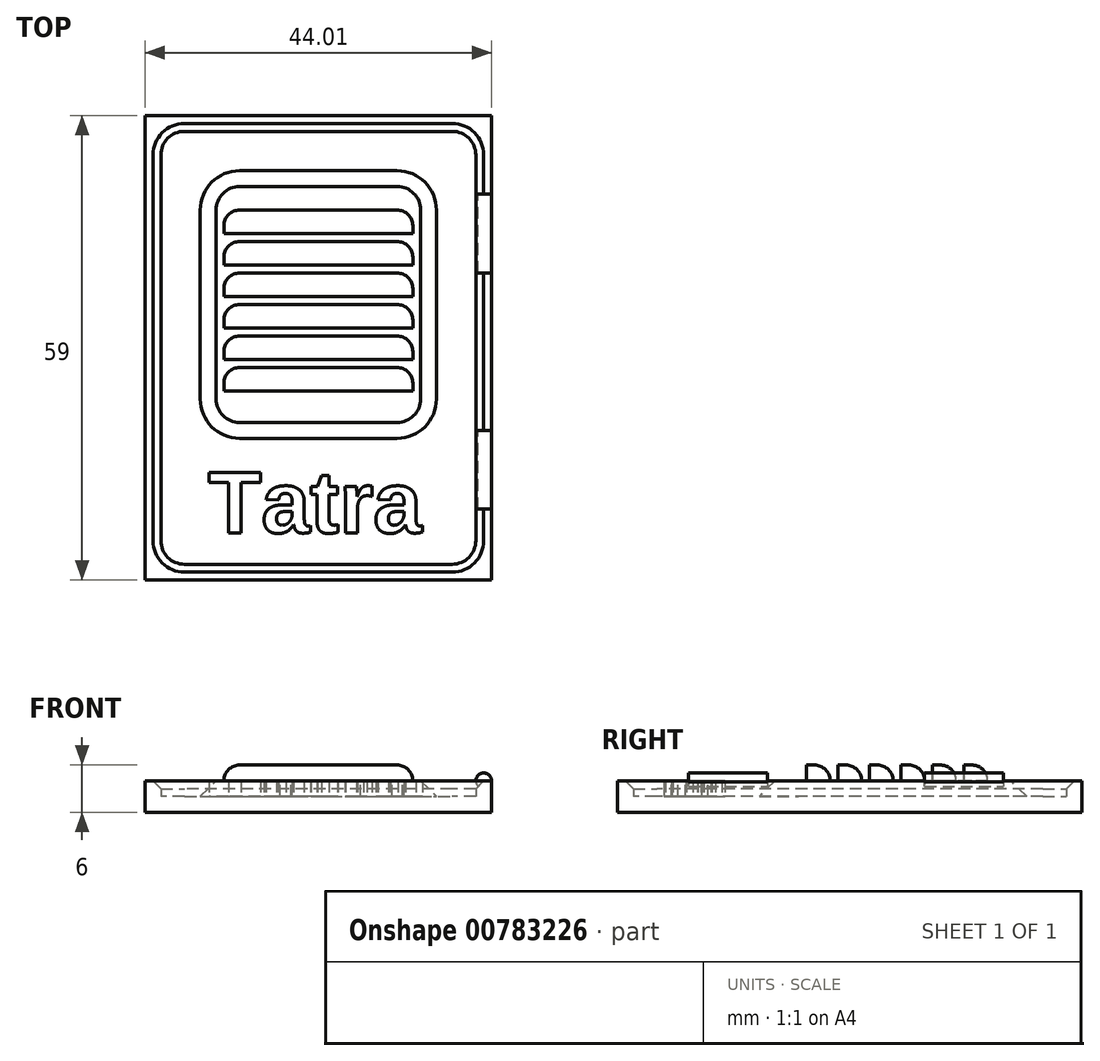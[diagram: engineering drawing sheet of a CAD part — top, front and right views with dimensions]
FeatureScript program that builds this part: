
annotation { "Feature Type Name" : "Feature", "Feature Type Description" : "" }
export const myFeature = defineFeature(function(context is Context, id is Id, definition is map)
    precondition{}
    {
        {
            var Q0;
            Q0=qCreatedBy(makeId("Top.planeOp"),FACE);
            var sketch = newSketch(context, id + "F0", { "sketchPlane" : qUnion([Q0])});
            skLineSegment(sketch, "E0.bottom", {"start": v(-26.46, 17) * mm, "end": v(17.54, 17) * mm});
            skLineSegment(sketch, "E0.top", {"start": v(-26.46, -42) * mm, "end": v(17.54, -42) * mm});
            skLineSegment(sketch, "E0.left", {"start": v(-26.46, 17) * mm, "end": v(-26.46, -42) * mm});
            skLineSegment(sketch, "E0.right", {"start": v(17.54, 17) * mm, "end": v(17.54, -42) * mm});
            skSolve(sketch);
        }
        {
            var Q0;
            Q0 = qSketchRegion(id + "F0", true);
            extrude(context, id + "F1", {"entities" : qUnion([Q0]), "depth" : 2 * mm, "offsetDistance" : 25 * mm});
        }
        {
            var Q0;
            Q0=makeQuery(id+"F1.opExtrude","CAP_FACE",FACE,{"disambiguationData":[OSD([sQuery(id+"F0.wireOp",EDGE,"E0.bottom"),sQuery(id+"F0.wireOp",EDGE,"E0.top"),sQuery(id+"F0.wireOp",EDGE,"E0.left"),sQuery(id+"F0.wireOp",EDGE,"E0.right")])],"isStart":false});
            var sketch = newSketch(context, id + "F2", { "sketchPlane" : qUnion([Q0])});
            skLineSegment(sketch, "E1.bottom", {"start": v(-26.46, 17) * mm, "end": v(17.54, 17) * mm});
            skLineSegment(sketch, "E1.top", {"start": v(-26.46, -42) * mm, "end": v(17.54, -42) * mm});
            skLineSegment(sketch, "E1.left", {"start": v(-26.46, 17) * mm, "end": v(-26.46, -42) * mm});
            skLineSegment(sketch, "E1.right", {"start": v(17.54, 17) * mm, "end": v(17.54, -42) * mm});
            skLineSegment(sketch, "E2.0", {"start": v(-24.46, 15) * mm, "end": v(-24.46, -40) * mm});
            skLineSegment(sketch, "E3.0", {"start": v(-24.46, 15) * mm, "end": v(15.54, 15) * mm});
            skLineSegment(sketch, "E4.0", {"start": v(15.54, 15) * mm, "end": v(15.54, -40) * mm});
            skLineSegment(sketch, "E5.0", {"start": v(-24.46, -40) * mm, "end": v(15.54, -40) * mm});
            skPoint(sketch, "E6", {"position": v(15.54, -22.21) * mm});
            skText(sketch, "E7", { "text": "Tatra", "fontName": "Arimo-Bold.ttf"});
            const initialGuessF2  = {"E7": [-0.02196, -0.038, 1, 0, 0.01]};
            skSetInitialGuess(sketch, initialGuessF2);
            skSolve(sketch);
        }
        {
            var Q0;
            Q0 = qSketchRegion(id + "F2", true);
            extrude(context, id + "F3", {"entities" : qUnion([Q0]), "operationType" : NewBodyOperationType.ADD, "depth" : 2 * mm, "offsetDistance" : 25 * mm});
        }
        {
            var Q0;
            Q0=makeQuery(id+"F1.opExtrude","CAP_FACE",FACE,{"disambiguationData":[OSD([sQuery(id+"F0.wireOp",EDGE,"E0.bottom"),sQuery(id+"F0.wireOp",EDGE,"E0.top"),sQuery(id+"F0.wireOp",EDGE,"E0.left"),sQuery(id+"F0.wireOp",EDGE,"E0.right")])],"isStart":false});
            var sketch = newSketch(context, id + "F4", { "sketchPlane" : qUnion([Q0])});
            skLineSegment(sketch, "E8.bottom", {"start": v(-14.46, 10) * mm, "end": v(5.54, 10) * mm});
            skLineSegment(sketch, "E8.top", {"start": v(-14.46, -24) * mm, "end": v(5.54, -24) * mm});
            skLineSegment(sketch, "E8.left", {"start": v(-19.46, 5) * mm, "end": v(-19.46, -19) * mm});
            skLineSegment(sketch, "E8.right", {"start": v(10.54, 5) * mm, "end": v(10.54, -19) * mm});
            skPoint(sketch, "E9.visualSharp", {"position": v(-19.46, 10) * mm});
            skArc(sketch, "E9.filletArc", {"start": v(-14.46, 10) * mm, "mid": v(-18, 8.53) * mm, "end": v(-19.46, 5) * mm});
            skPoint(sketch, "E10.visualSharp", {"position": v(10.54, 10) * mm});
            skArc(sketch, "E10.filletArc", {"start": v(10.54, 5) * mm, "mid": v(9.08, 8.53) * mm, "end": v(5.54, 10) * mm});
            skPoint(sketch, "E11.visualSharp", {"position": v(10.54, -24) * mm});
            skArc(sketch, "E11.filletArc", {"start": v(5.54, -24) * mm, "mid": v(9.08, -22.54) * mm, "end": v(10.54, -19) * mm});
            skPoint(sketch, "E12.visualSharp", {"position": v(-19.46, -24) * mm});
            skArc(sketch, "E12.filletArc", {"start": v(-19.46, -19) * mm, "mid": v(-18, -22.54) * mm, "end": v(-14.46, -24) * mm});
            skSolve(sketch);
        }
        {
            var Q0;
            Q0=makeQuery(id+"F4.imprint","IMPRINT",FACE,{"disambiguationData":[TD([[makeQuery(id+"F4.imprint","IMPRINT",EDGE,{"derivedFrom":sQuery(id+"F4.wireOp",EDGE,"E8.bottom")}),-1.0]])]});
            extrude(context, id + "F5", {"entities" : qUnion([Q0]), "operationType" : NewBodyOperationType.ADD, "depth" : 2 * mm, "offsetDistance" : 25 * mm});
        }
        {
            var Q0;
            Q0=makeQuery(id+"F5.opExtrude","CAP_FACE",FACE,{"disambiguationData":[OSD([sQuery(id+"F4.wireOp",EDGE,"E8.bottom"),sQuery(id+"F4.wireOp",EDGE,"E8.top"),sQuery(id+"F4.wireOp",EDGE,"E8.left"),sQuery(id+"F4.wireOp",EDGE,"E8.right"),sQuery(id+"F4.wireOp",EDGE,"E9.filletArc"),sQuery(id+"F4.wireOp",EDGE,"E10.filletArc"),sQuery(id+"F4.wireOp",EDGE,"E11.filletArc"),sQuery(id+"F4.wireOp",EDGE,"E12.filletArc")])],"isStart":false});
            var sketch = newSketch(context, id + "F6", { "sketchPlane" : qUnion([Q0])});
            skLineSegment(sketch, "E13.bottom", {"start": v(-14.46, 5) * mm, "end": v(5.54, 5) * mm});
            skLineSegment(sketch, "E13.left", {"start": v(-16.46, 3) * mm, "end": v(-16.46, 2) * mm});
            skLineSegment(sketch, "E13.right", {"start": v(7.54, 3) * mm, "end": v(7.54, 2) * mm});
            skLineSegment(sketch, "E14.0", {"start": v(-14.46, 1) * mm, "end": v(5.54, 1) * mm});
            skLineSegment(sketch, "E15.0", {"start": v(-14.46, -3) * mm, "end": v(5.54, -3) * mm});
            skLineSegment(sketch, "E16.0", {"start": v(-14.46, -7) * mm, "end": v(5.54, -7) * mm});
            skLineSegment(sketch, "E17.0", {"start": v(-14.46, -11) * mm, "end": v(5.54, -11) * mm});
            skPoint(sketch, "E18", {"position": v(-16.46, 1) * mm});
            skPoint(sketch, "E19", {"position": v(-16.46, -3) * mm});
            skPoint(sketch, "E20", {"position": v(-16.46, -7) * mm});
            skPoint(sketch, "E21", {"position": v(-16.46, -11) * mm});
            skPoint(sketch, "E22", {"position": v(-16.46, -15) * mm});
            skPoint(sketch, "E23", {"position": v(7.54, 5) * mm});
            skPoint(sketch, "E24", {"position": v(7.54, 1) * mm});
            skPoint(sketch, "E25", {"position": v(7.54, -3) * mm});
            skPoint(sketch, "E26", {"position": v(7.54, -7) * mm});
            skPoint(sketch, "E27", {"position": v(7.54, -11) * mm});
            skPoint(sketch, "E28", {"position": v(7.54, -15) * mm});
            skPoint(sketch, "E29", {"position": v(-16.46, 5) * mm});
            skLineSegment(sketch, "E30.0", {"start": v(-16.46, 2) * mm, "end": v(7.54, 2) * mm});
            skLineSegment(sketch, "E31.0", {"start": v(-16.46, -2) * mm, "end": v(7.54, -2) * mm});
            skLineSegment(sketch, "E32.0", {"start": v(-16.46, -6) * mm, "end": v(7.54, -6) * mm});
            skLineSegment(sketch, "E33.0", {"start": v(-16.46, -10) * mm, "end": v(7.54, -10) * mm});
            skLineSegment(sketch, "E34.0", {"start": v(-16.46, -14) * mm, "end": v(7.54, -14) * mm});
            skLineSegment(sketch, "E35", {"start": v(-14.46, -15) * mm, "end": v(5.54, -15) * mm});
            skLineSegment(sketch, "E36.trimOffspring", {"start": v(-16.46, -1) * mm, "end": v(-16.46, -2) * mm});
            skLineSegment(sketch, "E37.trimOffspring", {"start": v(-16.46, -5) * mm, "end": v(-16.46, -6) * mm});
            skLineSegment(sketch, "E38.trimOffspring", {"start": v(-16.46, -9) * mm, "end": v(-16.46, -10) * mm});
            skLineSegment(sketch, "E39.trimOffspring", {"start": v(-16.46, -13) * mm, "end": v(-16.46, -14) * mm});
            skLineSegment(sketch, "E40.0", {"start": v(-16.46, -18) * mm, "end": v(7.54, -18) * mm});
            skLineSegment(sketch, "E41.trimOffspring", {"start": v(7.54, -17) * mm, "end": v(7.54, -18) * mm});
            skLineSegment(sketch, "E42.trimOffspring", {"start": v(-16.46, -17) * mm, "end": v(-16.46, -18) * mm});
            skLineSegment(sketch, "E43.trimOffspring", {"start": v(7.54, -13) * mm, "end": v(7.54, -14) * mm});
            skLineSegment(sketch, "E44.trimOffspring", {"start": v(7.54, -9) * mm, "end": v(7.54, -10) * mm});
            skLineSegment(sketch, "E45.trimOffspring", {"start": v(7.54, -5) * mm, "end": v(7.54, -6) * mm});
            skLineSegment(sketch, "E46.trimOffspring", {"start": v(7.54, -1) * mm, "end": v(7.54, -2) * mm});
            skArc(sketch, "E47.filletArc", {"start": v(-14.46, 5) * mm, "mid": v(-15.87, 4.4) * mm, "end": v(-16.46, 3) * mm});
            skArc(sketch, "E48.filletArc", {"start": v(7.54, 3) * mm, "mid": v(6.96, 4.4) * mm, "end": v(5.54, 5) * mm});
            skArc(sketch, "E49.filletArc", {"start": v(-14.46, 1) * mm, "mid": v(-15.87, 0.4) * mm, "end": v(-16.46, -1) * mm});
            skArc(sketch, "E50.filletArc", {"start": v(-14.46, -3) * mm, "mid": v(-15.87, -3.6) * mm, "end": v(-16.46, -5) * mm});
            skArc(sketch, "E51.filletArc", {"start": v(-14.46, -7) * mm, "mid": v(-15.87, -7.6) * mm, "end": v(-16.46, -9) * mm});
            skArc(sketch, "E52.filletArc", {"start": v(-14.46, -11) * mm, "mid": v(-15.87, -11.6) * mm, "end": v(-16.46, -13) * mm});
            skArc(sketch, "E53.filletArc", {"start": v(-14.46, -15) * mm, "mid": v(-15.87, -15.6) * mm, "end": v(-16.46, -17) * mm});
            skArc(sketch, "E54.filletArc", {"start": v(7.54, -17) * mm, "mid": v(6.96, -15.6) * mm, "end": v(5.54, -15) * mm});
            skArc(sketch, "E55.filletArc", {"start": v(7.54, -13) * mm, "mid": v(6.96, -11.6) * mm, "end": v(5.54, -11) * mm});
            skArc(sketch, "E56.filletArc", {"start": v(7.54, -9) * mm, "mid": v(6.96, -7.6) * mm, "end": v(5.54, -7) * mm});
            skArc(sketch, "E57.filletArc", {"start": v(7.54, -5) * mm, "mid": v(6.96, -3.6) * mm, "end": v(5.54, -3) * mm});
            skArc(sketch, "E58.filletArc", {"start": v(7.54, -1) * mm, "mid": v(6.96, 0.4) * mm, "end": v(5.54, 1) * mm});
            skSolve(sketch);
        }
        {
            var Q0;
            Q0=makeQuery(id+"F6.imprint","IMPRINT",FACE,{"disambiguationData":[TD([[makeQuery(id+"F6.imprint","IMPRINT",EDGE,{"derivedFrom":sQuery(id+"F6.wireOp",EDGE,"E14.0")}),-1.0]])]});
            var Q1;
            Q1=makeQuery(id+"F6.imprint","IMPRINT",FACE,{"disambiguationData":[TD([[makeQuery(id+"F6.imprint","IMPRINT",EDGE,{"derivedFrom":sQuery(id+"F6.wireOp",EDGE,"E15.0")}),-1.0]])]});
            var Q2;
            Q2=makeQuery(id+"F6.imprint","IMPRINT",FACE,{"disambiguationData":[TD([[makeQuery(id+"F6.imprint","IMPRINT",EDGE,{"derivedFrom":sQuery(id+"F6.wireOp",EDGE,"E16.0")}),-1.0]])]});
            var Q3;
            Q3=makeQuery(id+"F6.imprint","IMPRINT",FACE,{"disambiguationData":[TD([[makeQuery(id+"F6.imprint","IMPRINT",EDGE,{"derivedFrom":sQuery(id+"F6.wireOp",EDGE,"E17.0")}),-1.0]])]});
            var Q4;
            Q4=makeQuery(id+"F6.imprint","IMPRINT",FACE,{"disambiguationData":[TD([[makeQuery(id+"F6.imprint","IMPRINT",EDGE,{"derivedFrom":sQuery(id+"F6.wireOp",EDGE,"E35")}),-1.0]])]});
            var Q5;
            Q5=makeQuery(id+"F6.imprint","IMPRINT",FACE,{"disambiguationData":[TD([[makeQuery(id+"F6.imprint","IMPRINT",EDGE,{"derivedFrom":sQuery(id+"F6.wireOp",EDGE,"E13.bottom")}),-1.0]])]});
            extrude(context, id + "F7", {"entities" : qUnion([Q0, Q1, Q2, Q3, Q4, Q5]), "operationType" : NewBodyOperationType.ADD, "depth" : 2 * mm, "offsetDistance" : 25 * mm});
        }
        {
            var Q0;
            Q0=qCreatedBy(makeId("Front.planeOp"),FACE);
            cPlane(context, id + "F8", {"entities" : qUnion([Q0]), "cplaneType" : CPlaneType.OFFSET, "offset" : 28 * mm, "width" : 150 * mm, "height" : 150 * mm});
        }
        {
            var Q0;
            Q0=qCreatedBy(id+"F8.planeOp",FACE);
            var sketch = newSketch(context, id + "F9", { "sketchPlane" : qUnion([Q0])});
            skCircle(sketch, "E59", {"center": v(16.55, 3.98) * mm, "radius": 1 * mm});
            skPoint(sketch, "E60.center.orphan", {"position": v(14.24, 3.98) * mm});
            skSolve(sketch);
        }
        {
            var Q0;
            Q0 = qSketchRegion(id + "F9", true);
            extrude(context, id + "F10", {"entities" : qUnion([Q0]), "operationType" : NewBodyOperationType.ADD, "endBound" : BoundingType.SYMMETRIC, "depth" : 10 * mm, "offsetDistance" : 25 * mm});
        }
        {
            var Q0;
            Q0=qCreatedBy(id+"F8.planeOp",FACE);
            cPlane(context, id + "F11", {"entities" : qUnion([Q0]), "cplaneType" : CPlaneType.OFFSET, "offset" : 30 * mm, "oppositeDirection" : true, "width" : 150 * mm, "height" : 150 * mm});
        }
        {
            var Q0;
            Q0=qCreatedBy(id+"F11.planeOp",FACE);
            var sketch = newSketch(context, id + "F12", { "sketchPlane" : qUnion([Q0])});
            skCircle(sketch, "E61", {"center": v(16.55, 4) * mm, "radius": 1 * mm});
            skSolve(sketch);
        }
        {
            var Q0;
            Q0 = qSketchRegion(id + "F12", true);
            extrude(context, id + "F13", {"entities" : qUnion([Q0]), "operationType" : NewBodyOperationType.ADD, "endBound" : BoundingType.SYMMETRIC, "depth" : 10 * mm, "offsetDistance" : 25 * mm});
        }
        {
            var Q0;
            Q0=makeQuery(id+"F5.opExtrude","CAP_EDGE",EDGE,{"disambiguationData":[OSD([sQuery(id+"F4.wireOp",EDGE,"E8.top")])],"isStart":false});
            chamfer(context, id + "F14", {"entities" : qUnion([Q0]), "width" : 2 * mm, "tangentPropagation" : true});
        }
        {
            var Q0;
            Q0=makeQuery(id+"F3.opExtrude","SWEPT_EDGE",EDGE,{"disambiguationData":[OSD([sQuery(id+"F2.wireOp",EDGE,"E2.0"),sQuery(id+"F2.wireOp",EDGE,"E3.0")])]});
            var Q1;
            Q1=makeQuery(id+"F3.opExtrude","SWEPT_EDGE",EDGE,{"disambiguationData":[OSD([sQuery(id+"F2.wireOp",EDGE,"E2.0"),sQuery(id+"F2.wireOp",EDGE,"E5.0")])]});
            var Q2;
            Q2=makeQuery(id+"F3.opExtrude","SWEPT_EDGE",EDGE,{"disambiguationData":[OSD([sQuery(id+"F2.wireOp",EDGE,"E4.0"),sQuery(id+"F2.wireOp",EDGE,"E5.0")])]});
            var Q3;
            Q3=makeQuery(id+"F3.opExtrude","SWEPT_EDGE",EDGE,{"disambiguationData":[OSD([sQuery(id+"F2.wireOp",EDGE,"E3.0"),sQuery(id+"F2.wireOp",EDGE,"E4.0")])]});
            fillet(context, id + "F15", {"entities" : qUnion([Q0, Q1, Q2, Q3]), "radius" : 3 * mm, "tangentPropagation" : true, "allowEdgeOverflow" : false});
        }
        {
            var Q0;
            Q0=makeQuery(id+"F3.opExtrude","CAP_EDGE",EDGE,{"disambiguationData":[OSD([sQuery(id+"F2.wireOp",EDGE,"E2.0")])],"isStart":false});
            chamfer(context, id + "F16", {"entities" : qUnion([Q0]), "width" : 1 * mm, "tangentPropagation" : true});
        }
        {
            var Q0;
            Q0=makeQuery(id+"F7.opExtrude","CAP_EDGE",EDGE,{"disambiguationData":[OSD([sQuery(id+"F6.wireOp",EDGE,"E13.bottom")])],"isStart":false});
            var Q1;
            Q1=makeQuery(id+"F7.opExtrude","CAP_EDGE",EDGE,{"disambiguationData":[OSD([sQuery(id+"F6.wireOp",EDGE,"E14.0")])],"isStart":false});
            var Q2;
            Q2=makeQuery(id+"F7.opExtrude","CAP_EDGE",EDGE,{"disambiguationData":[OSD([sQuery(id+"F6.wireOp",EDGE,"E15.0")])],"isStart":false});
            var Q3;
            Q3=makeQuery(id+"F7.opExtrude","CAP_EDGE",EDGE,{"disambiguationData":[OSD([sQuery(id+"F6.wireOp",EDGE,"E16.0")])],"isStart":false});
            var Q4;
            Q4=makeQuery(id+"F7.opExtrude","CAP_EDGE",EDGE,{"disambiguationData":[OSD([sQuery(id+"F6.wireOp",EDGE,"E17.0")])],"isStart":false});
            var Q5;
            Q5=makeQuery(id+"F7.opExtrude","CAP_EDGE",EDGE,{"disambiguationData":[OSD([sQuery(id+"F6.wireOp",EDGE,"E35")])],"isStart":false});
            fillet(context, id + "F17", {"entities" : qUnion([Q0, Q1, Q2, Q3, Q4, Q5]), "radius" : 2 * mm, "tangentPropagation" : true, "allowEdgeOverflow" : false});
        }
        {
            var Q0;
            Q0 = qSketchRegion(id + "F2", true);
            extrude(context, id + "F18", {"entities" : qUnion([Q0]), "operationType" : NewBodyOperationType.ADD, "depth" : 1 * mm, "offsetDistance" : 25 * mm});
        }
        {
            var Q0;
            Q0=makeQuery(id+"F1.opExtrude","CAP_FACE",FACE,{"disambiguationData":[OSD([sQuery(id+"F0.wireOp",EDGE,"E0.bottom"),sQuery(id+"F0.wireOp",EDGE,"E0.top"),sQuery(id+"F0.wireOp",EDGE,"E0.left"),sQuery(id+"F0.wireOp",EDGE,"E0.right")])],"isStart":false});
            var sketch = newSketch(context, id + "F19", { "sketchPlane" : qUnion([Q0])});
            skText(sketch, "E62", { "text": "Tatra", "fontName": "Arimo-Bold.ttf"});
            const initialGuessF19  = {"E62": [-0.01846, -0.036, 1, 0, 0.008]};
            skSetInitialGuess(sketch, initialGuessF19);
            skSolve(sketch);
        }
        {
            var Q0;
            Q0=makeQuery(id+"F19.imprint","IMPRINT",FACE,{"disambiguationData":[TD([[makeQuery(id+"F19.imprint","IMPRINT",EDGE,{"derivedFrom":sQuery(id+"F19.wireOp",EDGE,"E62.sketch_text.stroke-0")}),-1.0]])]});
            var Q1;
            Q1=makeQuery(id+"F19.imprint","IMPRINT",FACE,{"disambiguationData":[TD([[makeQuery(id+"F19.imprint","IMPRINT",EDGE,{"derivedFrom":sQuery(id+"F19.wireOp",EDGE,"E62.sketch_text.stroke-8")}),-1.0]])]});
            var Q2;
            Q2=makeQuery(id+"F19.imprint","IMPRINT",FACE,{"disambiguationData":[TD([[makeQuery(id+"F19.imprint","IMPRINT",EDGE,{"derivedFrom":sQuery(id+"F19.wireOp",EDGE,"E62.sketch_text.stroke-46")}),-1.0]])]});
            var Q3;
            Q3=makeQuery(id+"F19.imprint","IMPRINT",FACE,{"disambiguationData":[TD([[makeQuery(id+"F19.imprint","IMPRINT",EDGE,{"derivedFrom":sQuery(id+"F19.wireOp",EDGE,"E62.sketch_text.stroke-64")}),-1.0]])]});
            var Q4;
            Q4=makeQuery(id+"F19.imprint","IMPRINT",FACE,{"disambiguationData":[TD([[makeQuery(id+"F19.imprint","IMPRINT",EDGE,{"derivedFrom":sQuery(id+"F19.wireOp",EDGE,"E62.sketch_text.stroke-81")}),-1.0]])]});
            extrude(context, id + "F20", {"entities" : qUnion([Q0, Q1, Q2, Q3, Q4]), "operationType" : NewBodyOperationType.ADD, "depth" : 2 * mm, "offsetDistance" : 25 * mm});
        }
    });
